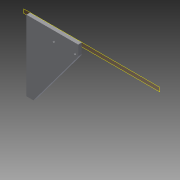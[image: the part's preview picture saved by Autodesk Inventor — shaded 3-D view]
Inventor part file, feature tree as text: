
AUTODESK INVENTOR PART (.ipt)
format: ipt  version: 2013 (Build 170138000, 138)  size: 80,384 bytes
history: native  units: in
note: dims shown in document units (in); Inventor stores cm internally (conversion verified against a paired STEP export)
features: reference x2, plane x1, extrude x1, sketch x1
ambient origin geometry x8: Origin, YZ Plane, XZ Plane, XY Plane, X Axis, Y Axis, Z Axis, Center Point
bodies: Solid1 (feature_tree)
feature tree (5):
  plane  "Work Plane1"
  extrude  "Extrusion1"  Depth=9.8425in
  sketch  "Sketch1"  dims[d0=0.9843in d2=9.8425in d3=0.5in d4=0.0in]
  reference  "Reference1"
  reference  "Reference2"
